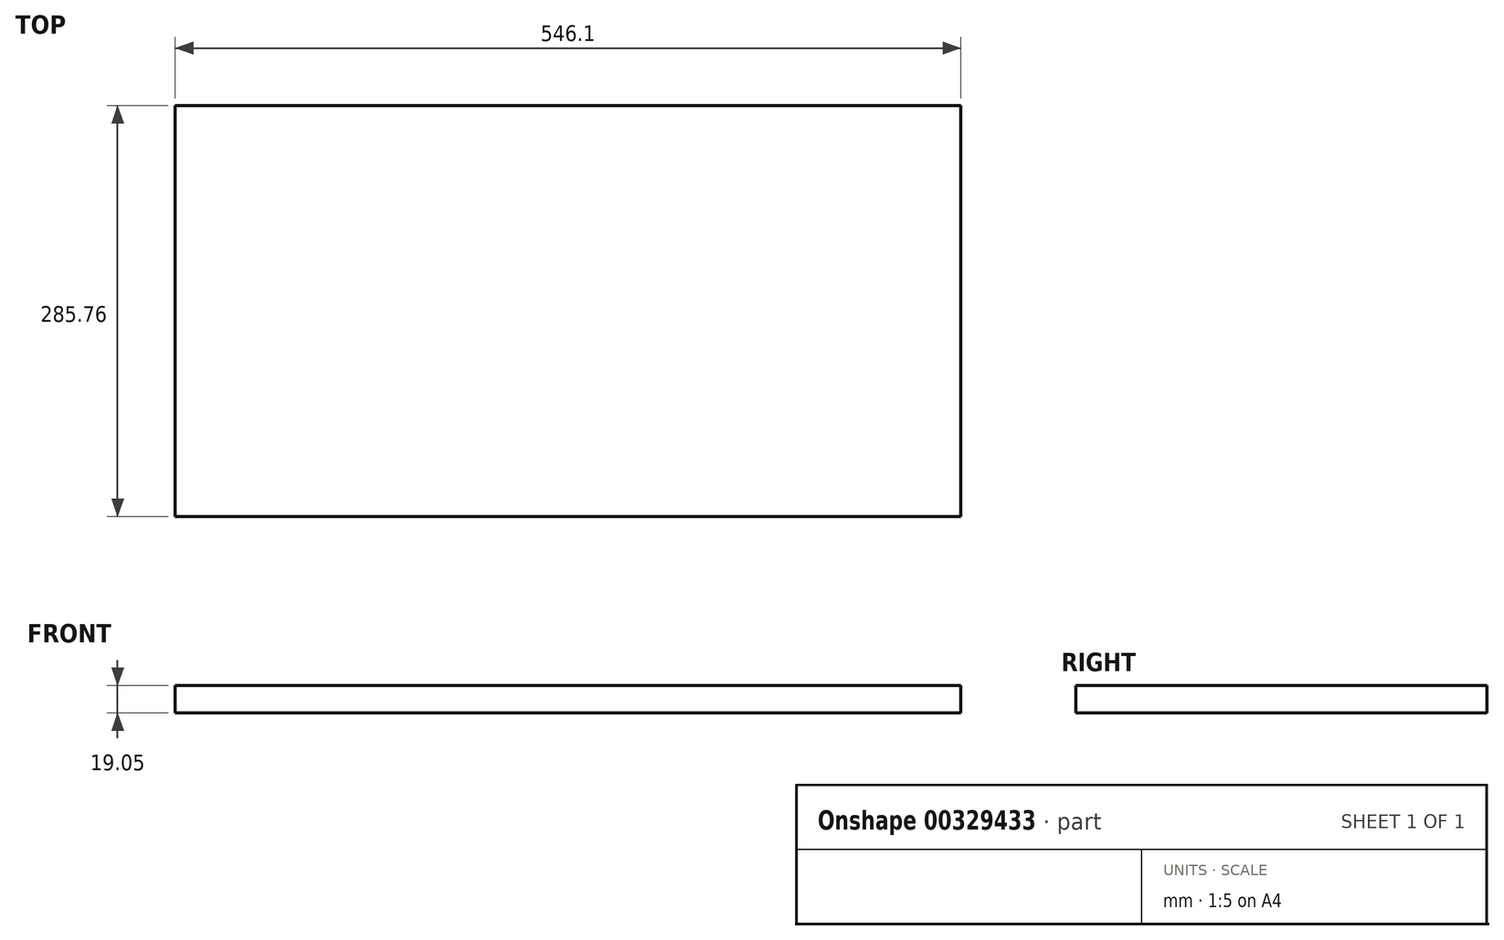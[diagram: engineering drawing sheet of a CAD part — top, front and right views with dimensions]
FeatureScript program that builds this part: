
annotation { "Feature Type Name" : "Feature", "Feature Type Description" : "" }
export const myFeature = defineFeature(function(context is Context, id is Id, definition is map)
    precondition{}
    {
        {
            var Q0;
            Q0=qCreatedBy(makeId("Top.planeOp"),FACE);
            var sketch = newSketch(context, id + "F0", { "sketchPlane" : qUnion([Q0])});
            skLineSegment(sketch, "E0.bottom", {"start": v(273.05, 142.88) * mm, "end": v(-273.05, 142.87) * mm});
            skLineSegment(sketch, "E0.top", {"start": v(273.05, -142.87) * mm, "end": v(-273.05, -142.88) * mm});
            skLineSegment(sketch, "E0.left", {"start": v(273.05, 142.88) * mm, "end": v(273.05, -142.87) * mm});
            skLineSegment(sketch, "E0.right", {"start": v(-273.05, 142.87) * mm, "end": v(-273.05, -142.88) * mm});
            skPoint(sketch, "E0.middle", {"position": v(0, 0) * mm});
            skSolve(sketch);
        }
        {
            var Q0;
            Q0=qSketchRegion(id+"F0",true);
            extrude(context, id + "F1", {"entities" : qUnion([Q0]), "depth" : 19.05 * mm});
        }
    });
